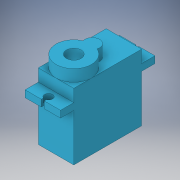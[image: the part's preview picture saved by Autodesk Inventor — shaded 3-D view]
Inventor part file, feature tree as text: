
AUTODESK INVENTOR PART (.ipt)
format: ipt  version: 2018 (Build 220112000, 112)  size: 170,496 bytes
history: native  units: in
note: dims shown in document units (in); Inventor stores cm internally (conversion verified against a paired STEP export)
features: extrude x6, sketch x6, mirror x2
ambient origin geometry x8: Origin, YZ Plane, XZ Plane, XY Plane, X Axis, Y Axis, Z Axis, Center Point
bodies: Solid1 (feature_tree)
feature tree (14):
  extrude  "Extrusion1"  Depth=0.9055in
  extrude  "Extrusion2"  Depth=0.6299in
  mirror  "Mirror1"
  extrude  "Extrusion3"  Depth=0.1772in TaperAngle=0.0deg
  mirror  "Mirror2"
  extrude  "Extrusion4"  Depth=0.2362in
  extrude  "Extrusion5"  Depth=0.0768in
  extrude  "Extrusion6"  Depth=0.3937in
  sketch  "Sketch1"  dims[d0=0.4724in d1=0.9055in]
  sketch  "Sketch2"  dims[d2=0.8858in d3=0.0in d4=0.6299in]
  sketch  "Sketch3"  dims[d5=0.0906in d6=0.1772in d7=0.0in]
  sketch  "Sketch4"  dims[d8=0.1063in d9=0.2362in]
  sketch  "Sketch5"  dims[d11=0.0197in d14=0.0768in]
  sketch  "Sketch6"  dims[d15=0.1772in d16=0.0in d17=0.1969in d18=0.1575in d19=0.0in d20=0.1969in d21=0.2461in d22=0.1575in d23=0.0in d24=0.3937in d25=0.0in]
